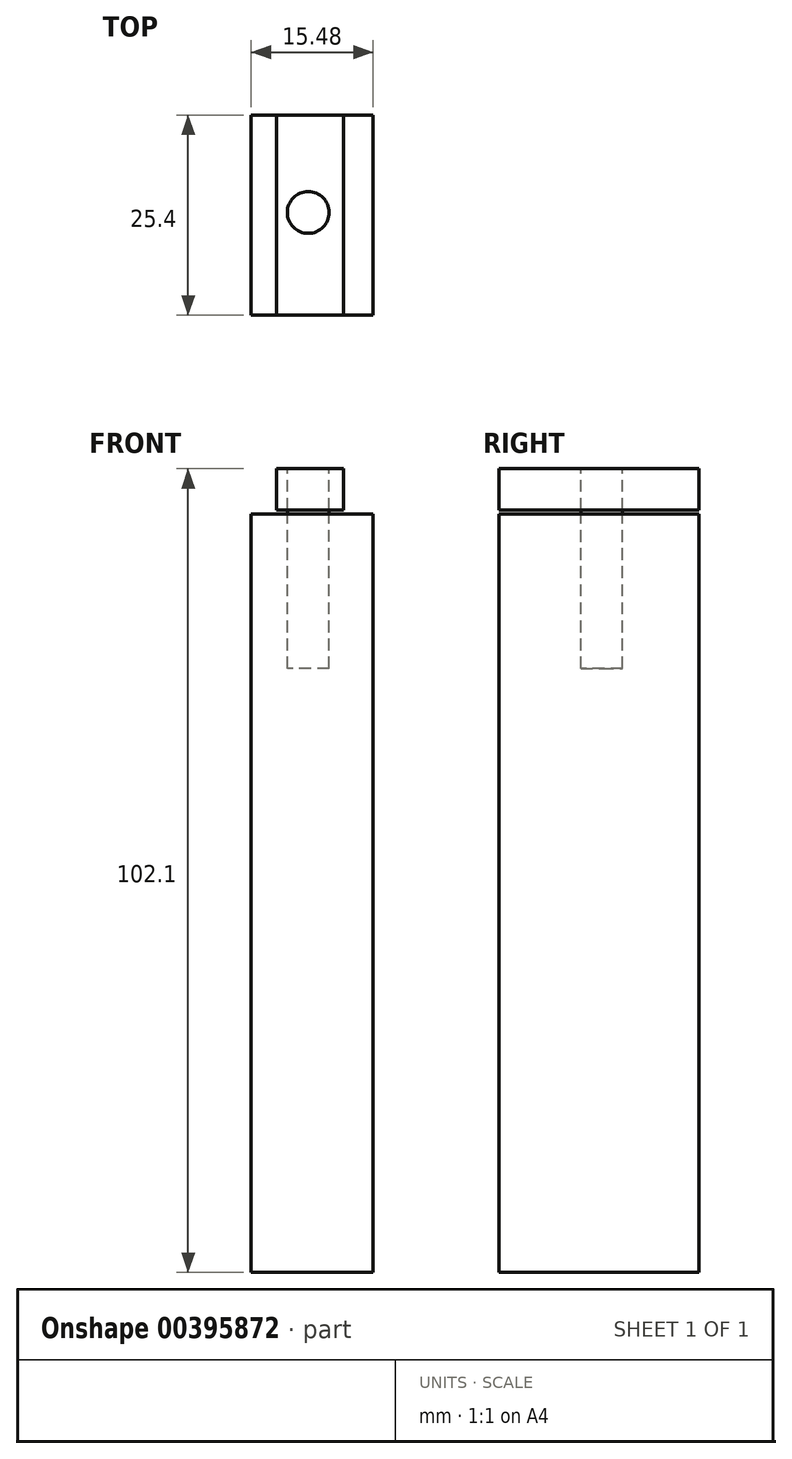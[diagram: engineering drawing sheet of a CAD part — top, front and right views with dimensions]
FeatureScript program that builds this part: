
annotation { "Feature Type Name" : "Feature", "Feature Type Description" : "" }
export const myFeature = defineFeature(function(context is Context, id is Id, definition is map)
    precondition{}
    {
        {
            var Q0;
            Q0=qCreatedBy(makeId("Front.planeOp"),FACE);
            var sketch = newSketch(context, id + "F0", { "sketchPlane" : qUnion([Q0])});
            skLineSegment(sketch, "E0.bottom", {"start": v(-7.49, 44.06) * mm, "end": v(7.99, 44.06) * mm});
            skLineSegment(sketch, "E0.top", {"start": v(-7.49, -52.3) * mm, "end": v(7.99, -52.3) * mm});
            skLineSegment(sketch, "E0.left", {"start": v(-7.49, 44.06) * mm, "end": v(-7.49, -52.3) * mm});
            skLineSegment(sketch, "E0.right", {"start": v(7.99, 44.06) * mm, "end": v(7.99, -52.3) * mm});
            skLineSegment(sketch, "E1.bottom", {"start": v(-4.24, 49.8) * mm, "end": v(4.24, 49.8) * mm});
            skLineSegment(sketch, "E1.top", {"start": v(-4.24, 44.56) * mm, "end": v(4.24, 44.56) * mm});
            skLineSegment(sketch, "E1.left", {"start": v(-4.24, 49.8) * mm, "end": v(-4.24, 44.56) * mm});
            skLineSegment(sketch, "E1.right", {"start": v(4.24, 49.8) * mm, "end": v(4.24, 44.56) * mm});
            skSolve(sketch);
        }
        {
            var Q0;
            Q0 = qSketchRegion(id + "F0", true);
            extrude(context, id + "F1", {"entities" : qUnion([Q0]), "depth" : 25.4 * mm});
        }
        {
            var Q0;
            Q0=makeQuery(id+"F1.opExtrude","SWEPT_FACE",FACE,{"disambiguationData":[OSD([sQuery(id+"F0.wireOp",EDGE,"E1.bottom")])]});
            var sketch = newSketch(context, id + "F2", { "sketchPlane" : qUnion([Q0])});
            skCircle(sketch, "E2", {"center": v(-0.25, -12.36) * mm, "radius": 2.65 * mm});
            skSolve(sketch);
        }
        {
            var Q0;
            Q0=makeQuery(id+"F2.imprint","IMPRINT",FACE,{"disambiguationData":[TD([[makeQuery(id+"F2.imprint","IMPRINT",EDGE,{"derivedFrom":sQuery(id+"F2.wireOp",EDGE,"E2")}),1.0]])]});
            extrude(context, id + "F3", {"entities" : qUnion([Q0]), "depth" : -25.4 * mm});
        }
    });
